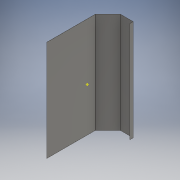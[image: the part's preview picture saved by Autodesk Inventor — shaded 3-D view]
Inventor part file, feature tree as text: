
AUTODESK INVENTOR PART (.ipt)
format: ipt  version: 2018 (Build 220112000, 112)  size: 130,048 bytes
history: native  units: mm
features: sheet_metal_op x3, other x2, sketch x1
ambient origin geometry x8: Origin, YZ Plane, XZ Plane, XY Plane, X Axis, Y Axis, Z Axis, Center Point
bodies: Solid1 (feature_tree)
feature tree (6):
  sheet_metal_op  "Contour Flange1"
  other  "Work Point1"
  sketch  "Sketch1"  dims[d3=154.0mm d4=1.6mm d5=1.6mm d6=0.8mm d7=3.2mm d8=1.6mm d9=1200.0mm d10=1.6mm d11=1.6mm d12=6.4mm d13=1.6mm d14=1.6mm d25=800.0mm d26=150.0mm d27=40.0mm d28=135.0deg d29=580.0mm d30=70.0mm]
  other  "Plate1"
  sheet_metal_op  "Bend1"
  sheet_metal_op  "Corner1"
